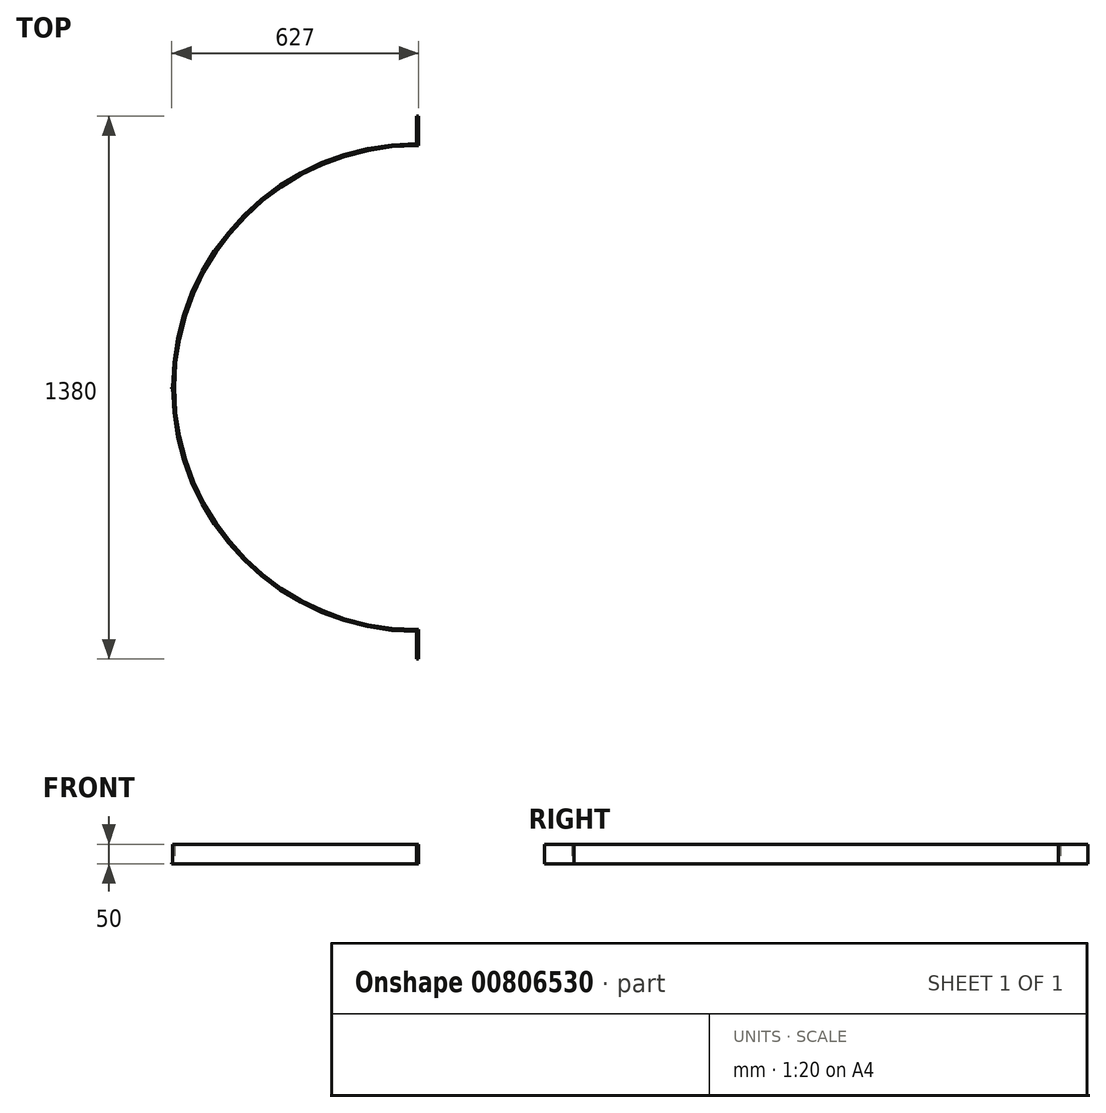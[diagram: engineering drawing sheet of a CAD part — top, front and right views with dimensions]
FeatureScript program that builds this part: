
annotation { "Feature Type Name" : "Feature", "Feature Type Description" : "" }
export const myFeature = defineFeature(function(context is Context, id is Id, definition is map)
    precondition{}
    {
        {
            var Q0;
            Q0=qCreatedBy(makeId("Top.planeOp"),FACE);
            var sketch = newSketch(context, id + "F0", { "sketchPlane" : qUnion([Q0])});
            skArc(sketch, "E0", {"start": v(-620, 0) * mm, "mid": v(-438.4, -438.4) * mm, "end": v(0, -620) * mm});
            skLineSegment(sketch, "E1", {"start": v(0, 0) * mm, "end": v(0, -620) * mm, "construction": true});
            skLineSegment(sketch, "E2", {"start": v(0, 0) * mm, "end": v(-620, 0) * mm, "construction": true});
            skArc(sketch, "E3.0", {"start": v(-615, 0) * mm, "mid": v(-434.87, -434.87) * mm, "end": v(0, -615) * mm});
            skLineSegment(sketch, "E4", {"start": v(0, -615) * mm, "end": v(0, -690) * mm});
            skLineSegment(sketch, "E5", {"start": v(0, -690) * mm, "end": v(5, -690) * mm});
            skLineSegment(sketch, "E6", {"start": v(5, -690) * mm, "end": v(5, -615) * mm});
            skLineSegment(sketch, "E7", {"start": v(5, -615) * mm, "end": v(0, -615) * mm});
            skLineSegment(sketch, "E8", {"start": v(-615, 0) * mm, "end": v(-620, 0) * mm});
            skSolve(sketch);
        }
        {
            var Q0;
            Q0=qSketchRegion(id+"F0",true);
            extrude(context, id + "F1", {"entities" : qUnion([Q0]), "depth" : 50 * mm, "offsetDistance" : 25 * mm});
        }
        {
            var Q0;
            Q0=makeQuery(id+"F1.opExtrude","SWEPT_BODY",BODY,{"disambiguationData":[OSD([sQuery(id+"F0.wireOp",EDGE,"E0"),sQuery(id+"F0.wireOp",EDGE,"E3.0"),sQuery(id+"F0.wireOp",EDGE,"E4"),sQuery(id+"F0.wireOp",EDGE,"E5"),sQuery(id+"F0.wireOp",EDGE,"E6"),sQuery(id+"F0.wireOp",EDGE,"E7"),sQuery(id+"F0.wireOp",EDGE,"E8")])]});
            var Q1;
            Q1=makeQuery(id+"F1.opExtrude","SWEPT_FACE",FACE,{"disambiguationData":[OSD([sQuery(id+"F0.wireOp",EDGE,"E8")])]});
            mirror(context, id + "F2", {"operationType" : NewBodyOperationType.ADD, "entities" : qUnion([Q0]), "mirrorPlane" : qUnion([Q1])});
        }
        {
            var Q0;
            Q0=qCreatedBy(makeId("Front.planeOp"),FACE);
            var sketch = newSketch(context, id + "F3", { "sketchPlane" : qUnion([Q0])});
            skLineSegment(sketch, "E9", {"start": v(0, 0) * mm, "end": v(-620, 0) * mm});
            skLineSegment(sketch, "E10", {"start": v(-620, 0) * mm, "end": v(-622, 0) * mm});
            skLineSegment(sketch, "E11", {"start": v(-622, 0) * mm, "end": v(-622, 2) * mm});
            skLineSegment(sketch, "E12", {"start": v(-622, 2) * mm, "end": v(-620, 2) * mm});
            skLineSegment(sketch, "E13", {"start": v(-620, 2) * mm, "end": v(-620, 0) * mm});
            skSolve(sketch);
        }
        {
            var Q0;
            Q0 = qSketchRegion(id + "F3", true);
            extrude(context, id + "F4", {"entities" : qUnion([Q0]), "depth" : 2 * mm, "offsetDistance" : 25 * mm});
        }
    });
